FCSTD DOCUMENT  (FreeCAD 0.16R6712 (Git))
Label: mapa_argentina
License: CreativeCommons Attribution-ShareAlike
LicenseURL: http://creativecommons.org/licenses/by-sa/4.0/
objects: Part::Feature×6, Part::Extrusion×6, App::DocumentObjectGroup×1
note: 12 computed .brp shape members not serialized (recipe doc carries the construction recipe); baked Part::Feature solids carry a one-line shape summary decoded from their .brp

FEATURE [App::DocumentObjectGroup] svgsymbols
FEATURE [Part::Feature] path7721
  shape: bbox 2.103 x 1.298 x 2e-07 mm, 0 faces, 0 solids (baked)
FEATURE [Part::Feature] path7721001
  shape: bbox 9.566 x 8.942 x 2e-07 mm, 0 faces, 0 solids (baked)
FEATURE [Part::Feature] path7721002
  shape: bbox 9.475 x 7.014 x 2e-07 mm, 0 faces, 0 solids (baked)
FEATURE [Part::Feature] path7721003
  shape: bbox 4.836 x 1.709 x 2e-07 mm, 0 faces, 0 solids (baked)
FEATURE [Part::Feature] path7721004
  shape: bbox 17.65 x 20.65 x 2e-07 mm, 0 faces, 0 solids (baked)
FEATURE [Part::Feature] path7721005
  shape: bbox 101 x 199.5 x 2e-07 mm, 0 faces, 0 solids (baked)
FEATURE [Part::Extrusion] Extrude006
  Base = -> path7721
  Dir = (0,0,5)
  Solid = true
FEATURE [Part::Extrusion] Extrude007
  Base = -> path7721001
  Dir = (0,0,5)
  Solid = true
FEATURE [Part::Extrusion] Extrude008
  Base = -> path7721002
  Dir = (0,0,5)
  Solid = true
FEATURE [Part::Extrusion] Extrude009
  Base = -> path7721003
  Dir = (0,0,5)
  Solid = true
FEATURE [Part::Extrusion] Extrude010
  Base = -> path7721004
  Dir = (0,0,5)
  Solid = true
FEATURE [Part::Extrusion] Extrude011
  Base = -> path7721005
  Dir = (0,0,5)
  Solid = true
